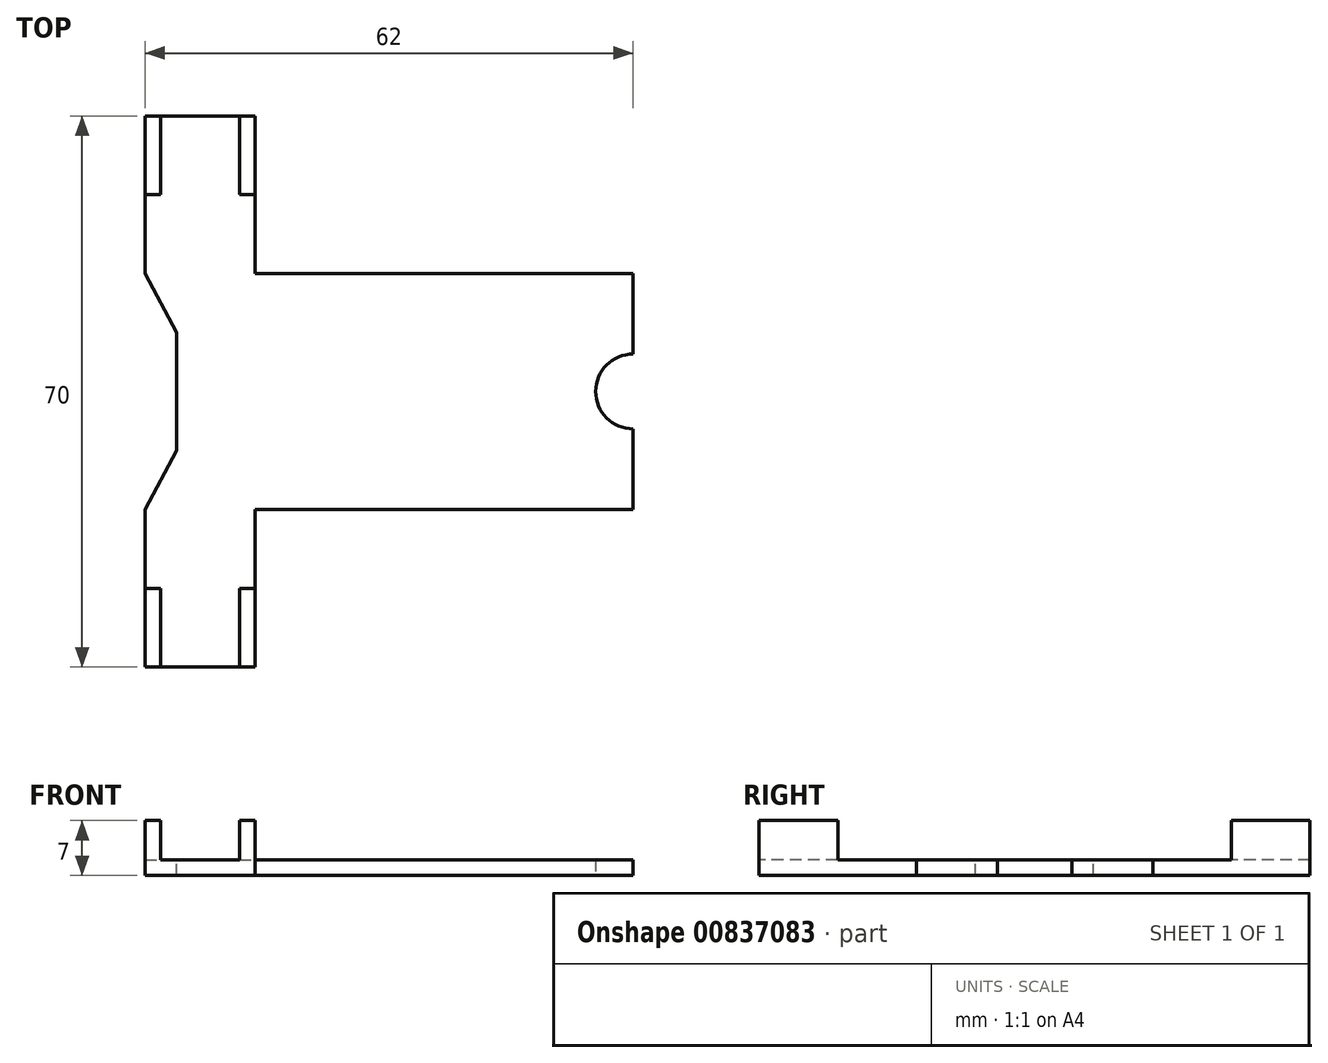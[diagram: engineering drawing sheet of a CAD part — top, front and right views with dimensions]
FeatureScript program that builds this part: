
annotation { "Feature Type Name" : "Feature", "Feature Type Description" : "" }
export const myFeature = defineFeature(function(context is Context, id is Id, definition is map)
    precondition{}
    {
        {
            var Q0;
            Q0=qCreatedBy(makeId("Top.planeOp"),FACE);
            var sketch = newSketch(context, id + "F0", { "sketchPlane" : qUnion([Q0])});
            skLineSegment(sketch, "E0.bottom", {"start": v(-48, 15) * mm, "end": v(0, 15) * mm});
            skLineSegment(sketch, "E0.top", {"start": v(-48, -15) * mm, "end": v(0, -15) * mm});
            skPoint(sketch, "E0.middle", {"position": v(0, 0) * mm});
            skLineSegment(sketch, "E1", {"start": v(-70.02, 0) * mm, "end": v(68.6, 0) * mm, "construction": true});
            skArc(sketch, "E2", {"start": v(0, 11) * mm, "mid": v(-11, 0) * mm, "end": v(0, -11) * mm, "construction": true});
            skArc(sketch, "E3", {"start": v(0, 4.75) * mm, "mid": v(-4.75, 0) * mm, "end": v(0, -4.75) * mm});
            skLineSegment(sketch, "E4", {"start": v(-48, 15) * mm, "end": v(-48, 35) * mm});
            skLineSegment(sketch, "E5", {"start": v(-48, 35) * mm, "end": v(-62, 35) * mm});
            skLineSegment(sketch, "E6", {"start": v(-62, 35) * mm, "end": v(-62, -35) * mm});
            skLineSegment(sketch, "E7", {"start": v(-62, -35) * mm, "end": v(-48, -35) * mm});
            skLineSegment(sketch, "E8", {"start": v(-48, -35) * mm, "end": v(-48, -15) * mm});
            skLineSegment(sketch, "E9", {"start": v(0, 15) * mm, "end": v(0, -15) * mm});
            skLineSegment(sketch, "E10", {"start": v(-60, 35) * mm, "end": v(-60, 25) * mm});
            skLineSegment(sketch, "E11", {"start": v(-50, 35) * mm, "end": v(-50, 25) * mm});
            skLineSegment(sketch, "E12", {"start": v(-62, -25) * mm, "end": v(-60, -25) * mm});
            skLineSegment(sketch, "E13.trimOffspring", {"start": v(-50, -25) * mm, "end": v(-48, -25) * mm});
            skLineSegment(sketch, "E14", {"start": v(-62, 25) * mm, "end": v(-60, 25) * mm});
            skLineSegment(sketch, "E15.trimOffspring", {"start": v(-50, 25) * mm, "end": v(-48, 25) * mm});
            skLineSegment(sketch, "E16", {"start": v(0, 39.66) * mm, "end": v(0, -51.4) * mm, "construction": true});
            skLineSegment(sketch, "E17.trimOffspring", {"start": v(-60, -25) * mm, "end": v(-60, -35) * mm});
            skLineSegment(sketch, "E18.trimOffspring", {"start": v(-50, -25) * mm, "end": v(-50, -35) * mm});
            skLineSegment(sketch, "E19", {"start": v(-60, 35) * mm, "end": v(-50, 25) * mm, "construction": true});
            skLineSegment(sketch, "E20", {"start": v(-50, 35) * mm, "end": v(-60, 25) * mm, "construction": true});
            skPoint(sketch, "E21", {"position": v(-55, 30) * mm});
            skLineSegment(sketch, "E22", {"start": v(-60, -25) * mm, "end": v(-50, -35) * mm, "construction": true});
            skLineSegment(sketch, "E23", {"start": v(-50, -25) * mm, "end": v(-60, -35) * mm, "construction": true});
            skPoint(sketch, "E24", {"position": v(-55, -30) * mm});
            skSolve(sketch);
        }
        {
            var Q0;
            {var subQ3=sQuery(id+"F0.wireOp",EDGE,"E0.bottom");Q0=makeQuery(id+"F0.imprint","IMPRINT",FACE,{"disambiguationData":[TD([[makeQuery(id+"F0.imprint","IMPRINT",EDGE,{"derivedFrom":subQ3}),-1.0]])]});}
            extrude(context, id + "F1", {"entities" : qUnion([Q0]), "depth" : 2 * mm, "offsetDistance" : 25 * mm});
        }
        {
            var Q0;
            {var subQ3=sQuery(id+"F0.wireOp",EDGE,"E10");Q0=makeQuery(id+"F0.imprint","IMPRINT",FACE,{"disambiguationData":[TD([[makeQuery(id+"F0.imprint","IMPRINT",EDGE,{"derivedFrom":subQ3}),-1.0]])]});}
            var Q1;
            {var subQ4=sQuery(id+"F0.wireOp",EDGE,"E11");Q1=makeQuery(id+"F0.imprint","IMPRINT",FACE,{"disambiguationData":[TD([[makeQuery(id+"F0.imprint","IMPRINT",EDGE,{"derivedFrom":subQ4}),1.0]])]});}
            var Q2;
            {var subQ3=sQuery(id+"F0.wireOp",EDGE,"E12");Q2=makeQuery(id+"F0.imprint","IMPRINT",FACE,{"disambiguationData":[TD([[makeQuery(id+"F0.imprint","IMPRINT",EDGE,{"derivedFrom":subQ3}),-1.0]])]});}
            var Q3;
            {var subQ4=sQuery(id+"F0.wireOp",EDGE,"E13.trimOffspring");Q3=makeQuery(id+"F0.imprint","IMPRINT",FACE,{"disambiguationData":[TD([[makeQuery(id+"F0.imprint","IMPRINT",EDGE,{"derivedFrom":subQ4}),-1.0]])]});}
            extrude(context, id + "F2", {"entities" : qUnion([Q0, Q1, Q2, Q3]), "operationType" : NewBodyOperationType.ADD, "depth" : 7 * mm, "offsetDistance" : 25 * mm});
        }
        {
            var Q0;
            Q0=makeQuery(id+"F1.opExtrude","CAP_FACE",FACE,{"disambiguationData":[OSD([sQuery(id+"F0.wireOp",EDGE,"E0.bottom"),sQuery(id+"F0.wireOp",EDGE,"E0.top"),sQuery(id+"F0.wireOp",EDGE,"E3"),sQuery(id+"F0.wireOp",EDGE,"E4"),sQuery(id+"F0.wireOp",EDGE,"E5"),sQuery(id+"F0.wireOp",EDGE,"E6"),sQuery(id+"F0.wireOp",EDGE,"E7"),sQuery(id+"F0.wireOp",EDGE,"E8"),sQuery(id+"F0.wireOp",EDGE,"E9"),sQuery(id+"F0.wireOp",EDGE,"E10"),sQuery(id+"F0.wireOp",EDGE,"E11"),sQuery(id+"F0.wireOp",EDGE,"E12"),sQuery(id+"F0.wireOp",EDGE,"E13.trimOffspring"),sQuery(id+"F0.wireOp",EDGE,"E14"),sQuery(id+"F0.wireOp",EDGE,"E15.trimOffspring"),sQuery(id+"F0.wireOp",EDGE,"E17.trimOffspring"),sQuery(id+"F0.wireOp",EDGE,"E18.trimOffspring")])],"isStart":false});
            var sketch = newSketch(context, id + "F3", { "sketchPlane" : qUnion([Q0])});
            skArc(sketch, "E25", {"start": v(0, 11) * mm, "mid": v(-11, 0) * mm, "end": v(0, -11) * mm});
            skArc(sketch, "E26", {"start": v(0, 12) * mm, "mid": v(-12, 0) * mm, "end": v(0, -12) * mm});
            skLineSegment(sketch, "E27", {"start": v(0, 15) * mm, "end": v(0, -18.54) * mm, "construction": true});
            skSolve(sketch);
        }
        {
            var Q0;
            {var subQ0=sQuery(id+"F0.wireOp",EDGE,"E12");var subQ1=sQuery(id+"F0.wireOp",EDGE,"E10");var subQ2=sQuery(id+"F0.wireOp",EDGE,"E8");var subQ3=sQuery(id+"F0.wireOp",EDGE,"E7");var subQ4=sQuery(id+"F0.wireOp",EDGE,"E18.trimOffspring");var subQ5=sQuery(id+"F0.wireOp",EDGE,"E6");var subQ7=sQuery(id+"F0.wireOp",EDGE,"E17.trimOffspring");var subQ8=sQuery(id+"F0.wireOp",EDGE,"E5");var subQ10=sQuery(id+"F0.wireOp",EDGE,"E14");var subQ11=sQuery(id+"F0.wireOp",EDGE,"E4");var subQ12=sQuery(id+"F0.wireOp",EDGE,"E11");var subQ13=sQuery(id+"F0.wireOp",EDGE,"E0.top");var subQ15=sQuery(id+"F0.wireOp",EDGE,"E9");var subQ16=sQuery(id+"F0.wireOp",EDGE,"E0.bottom");var subQ17=sQuery(id+"F0.wireOp",EDGE,"E3");var subQ21=sQuery(id+"F0.wireOp",EDGE,"E13.trimOffspring");var subQ23=sQuery(id+"F0.wireOp",EDGE,"E15.trimOffspring");Q0=makeQuery(id+"FWtAU8EWBhwUtOe_1.boolean.opBoolean","SPLIT",FACE,{"disambiguationData":[TD([makeQuery(id+"F1.opExtrude","SWEPT_FACE",FACE,{"disambiguationData":[OSD([subQ16])]})])],"derivedFrom":makeQuery(id+"F1.opExtrude","CAP_FACE",FACE,{"disambiguationData":[OSD([subQ16,subQ13,subQ17,subQ11,subQ8,subQ5,subQ3,subQ2,subQ15,subQ1,subQ12,subQ0,subQ21,subQ10,subQ23,subQ7,subQ4])],"isStart":false})});}
            var sketch = newSketch(context, id + "F4", { "sketchPlane" : qUnion([Q0])});
            skLineSegment(sketch, "E28", {"start": v(0, 0) * mm, "end": v(-99.46, 0) * mm, "construction": true});
            skLineSegment(sketch, "E29", {"start": v(0, 0) * mm, "end": v(0, 42) * mm, "construction": true});
            skLineSegment(sketch, "E30", {"start": v(-100.52, 7.5) * mm, "end": v(-36.1, 7.5) * mm, "construction": true});
            skLineSegment(sketch, "E31", {"start": v(-99.46, -7.5) * mm, "end": v(-14, -7.5) * mm, "construction": true});
            skLineSegment(sketch, "E32", {"start": v(-48, 15) * mm, "end": v(-62, 15) * mm, "construction": true});
            skLineSegment(sketch, "E33", {"start": v(-48, -15) * mm, "end": v(-62, -15) * mm, "construction": true});
            skLineSegment(sketch, "E34", {"start": v(-58, 37.98) * mm, "end": v(-58, -38.26) * mm, "construction": true});
            skLineSegment(sketch, "E35", {"start": v(-62, -15) * mm, "end": v(-58, -7.5) * mm});
            skLineSegment(sketch, "E36", {"start": v(-58, -7.5) * mm, "end": v(-58, 7.5) * mm});
            skLineSegment(sketch, "E37", {"start": v(-58, 7.5) * mm, "end": v(-62, 15) * mm});
            skLineSegment(sketch, "E38", {"start": v(-44, 35.32) * mm, "end": v(-44, -24.8) * mm, "construction": true});
            skLineSegment(sketch, "E39", {"start": v(-14, 36.69) * mm, "end": v(-14, -26.17) * mm, "construction": true});
            skArc(sketch, "E40", {"start": v(-14, 7.5) * mm, "mid": v(-10.32, 12.08) * mm, "end": v(-5.22, 15) * mm});
            skLineSegment(sketch, "E41", {"start": v(-48, 15) * mm, "end": v(-48, -15) * mm, "construction": true});
            skLineSegment(sketch, "E42", {"start": v(-40.5, 27.4) * mm, "end": v(-40.5, -19.77) * mm, "construction": true});
            skArc(sketch, "E43", {"start": v(-48, 15) * mm, "mid": v(-45.8, 9.7) * mm, "end": v(-40.5, 7.5) * mm});
            skLineSegment(sketch, "E44", {"start": v(-14, 7.5) * mm, "end": v(-40.5, 7.5) * mm});
            skArc(sketch, "E45.MirrorCS", {"start": v(-48, -15) * mm, "mid": v(-45.8, -9.7) * mm, "end": v(-40.5, -7.5) * mm});
            skLineSegment(sketch, "E46.MirrorCS", {"start": v(-14, -7.5) * mm, "end": v(-40.5, -7.5) * mm});
            skArc(sketch, "E47.MirrorCS", {"start": v(-14, -7.5) * mm, "mid": v(-10.32, -12.08) * mm, "end": v(-5.22, -15) * mm});
            skSolve(sketch);
        }
        {
            var Q0;
            {var subQ0=sQuery(id+"F4.wireOp",EDGE,"E35");Q0=makeQuery(id+"F4.imprint","IMPRINT",FACE,{"disambiguationData":[TD([[makeQuery(id+"F4.imprint","IMPRINT",EDGE,{"derivedFrom":subQ0}),1.0]])]});}
            extrude(context, id + "F5", {"entities" : qUnion([Q0]), "operationType" : NewBodyOperationType.REMOVE, "oppositeDirection" : true, "depth" : 25 * mm, "offsetDistance" : 25 * mm});
        }
    });
